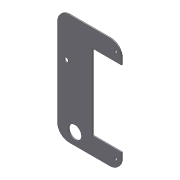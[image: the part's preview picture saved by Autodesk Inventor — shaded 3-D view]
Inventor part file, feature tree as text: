
AUTODESK INVENTOR PART (.ipt)
format: ipt  version: 2012 (Build 160160000, 160)  size: 103,424 bytes
history: native  units: in
note: dims shown in document units (in); Inventor stores cm internally (conversion verified against a paired STEP export)
features: extrude x1, fillet x1, sketch x1
ambient origin geometry x8: Origin, YZ Plane, XZ Plane, XY Plane, X Axis, Y Axis, Z Axis, Center Point
bodies: Solid1 (feature_tree)
feature tree (3):
  extrude  "Extrusion1"  Depth=1.5in
  fillet  "Fillet1"  Radius=9.5in
  sketch  "Sketch1"  dims[d0=1.5in d1=1.5in d2=9.5in d3=5.5in d4=0.5in d5=0.5in d6=0.25in d7=0.25in d8=0.75in d9=0.75in d10=2.5in d11=0.375in d12=0.75in d13=4.0in d14=1.125in d15=1.5in d16=1.0in d17=0.0938in d18=0.0in d19=1.0in]
